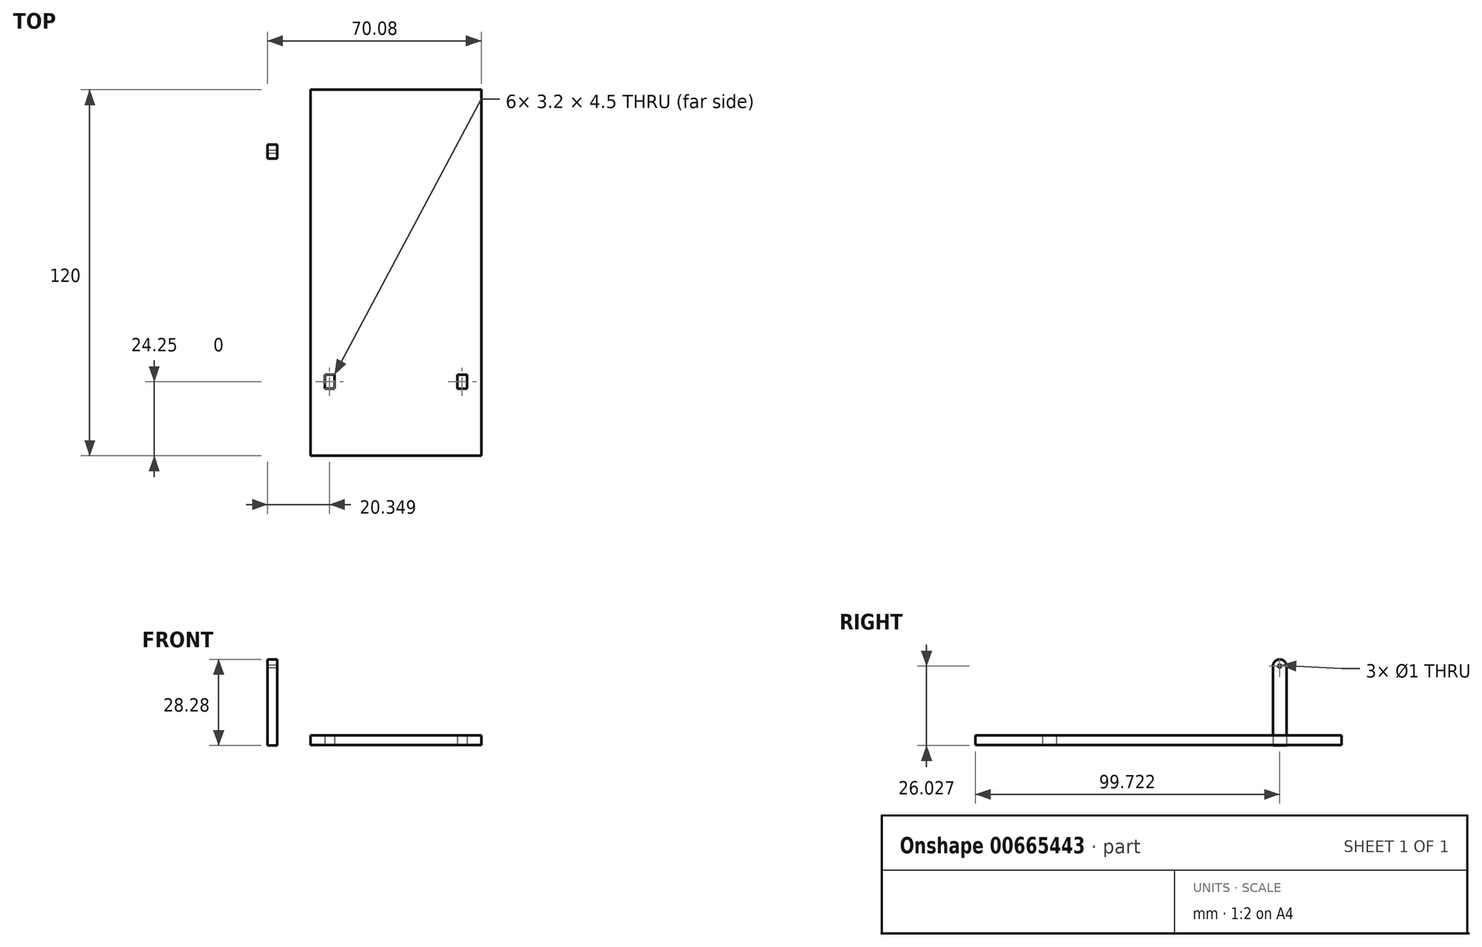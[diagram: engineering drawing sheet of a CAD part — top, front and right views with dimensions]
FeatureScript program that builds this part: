
annotation { "Feature Type Name" : "Feature", "Feature Type Description" : "" }
export const myFeature = defineFeature(function(context is Context, id is Id, definition is map)
    precondition{}
    {
        {
            var Q0;
            Q0=qCreatedBy(makeId("Right.planeOp"),FACE);
            var sketch = newSketch(context, id + "F0", { "sketchPlane" : qUnion([Q0])});
            skLineSegment(sketch, "E0.top", {"start": v(-22.53, -0.22) * mm, "end": v(-18.03, -0.22) * mm});
            skArc(sketch, "E1", {"start": v(-22.53, 25.8) * mm, "mid": v(-20.28, 28.06) * mm, "end": v(-18.03, 25.8) * mm});
            skLineSegment(sketch, "E2", {"start": v(-22.53, 25.8) * mm, "end": v(-22.53, -0.22) * mm});
            skLineSegment(sketch, "E3", {"start": v(-18.03, 25.8) * mm, "end": v(-18.03, -0.22) * mm});
            skCircle(sketch, "E4", {"center": v(-20.28, 25.8) * mm, "radius": 0.5 * mm});
            skSolve(sketch);
        }
        {
            var Q0;
            Q0=makeQuery(id+"F0.imprint","IMPRINT",FACE,{"disambiguationData":[TD([[makeQuery(id+"F0.imprint","IMPRINT",EDGE,{"derivedFrom":sQuery(id+"F0.wireOp",EDGE,"E0.top")}),1.0]])]});
            extrude(context, id + "F1", {"entities" : qUnion([Q0]), "oppositeDirection" : true, "depth" : 3.18 * mm, "offsetDistance" : 25 * mm});
        }
        {
            var Q0;
            Q0=qCreatedBy(makeId("Top.planeOp"),FACE);
            var sketch = newSketch(context, id + "F2", { "sketchPlane" : qUnion([Q0])});
            skLineSegment(sketch, "E5.bottom", {"start": v(10.9, 0) * mm, "end": v(66.9, 0) * mm});
            skLineSegment(sketch, "E5.top", {"start": v(10.9, -120) * mm, "end": v(66.9, -120) * mm});
            skLineSegment(sketch, "E5.left", {"start": v(10.9, 0) * mm, "end": v(10.9, -120) * mm});
            skLineSegment(sketch, "E5.right", {"start": v(66.9, 0) * mm, "end": v(66.9, -120) * mm});
            skLineSegment(sketch, "E6.bottom", {"start": v(18.77, -93.5) * mm, "end": v(15.57, -93.5) * mm});
            skLineSegment(sketch, "E6.top", {"start": v(18.77, -98) * mm, "end": v(15.57, -98) * mm});
            skLineSegment(sketch, "E6.left", {"start": v(18.77, -93.5) * mm, "end": v(18.77, -98) * mm});
            skLineSegment(sketch, "E6.right", {"start": v(15.57, -93.5) * mm, "end": v(15.57, -98) * mm});
            skPoint(sketch, "E6.middle", {"position": v(17.17, -95.75) * mm});
            skLineSegment(sketch, "E7.bottom", {"start": v(62.23, -93.5) * mm, "end": v(59.03, -93.5) * mm});
            skLineSegment(sketch, "E7.top", {"start": v(62.23, -98) * mm, "end": v(59.03, -98) * mm});
            skLineSegment(sketch, "E7.left", {"start": v(62.23, -93.5) * mm, "end": v(62.23, -98) * mm});
            skLineSegment(sketch, "E7.right", {"start": v(59.03, -93.5) * mm, "end": v(59.03, -98) * mm});
            skPoint(sketch, "E7.middle", {"position": v(60.63, -95.75) * mm});
            skSolve(sketch);
        }
        {
            var Q0;
            Q0 = qSketchRegion(id + "F2", true);
            extrude(context, id + "F3", {"entities" : qUnion([Q0]), "depth" : 3.18 * mm, "offsetDistance" : 25 * mm});
        }
    });
